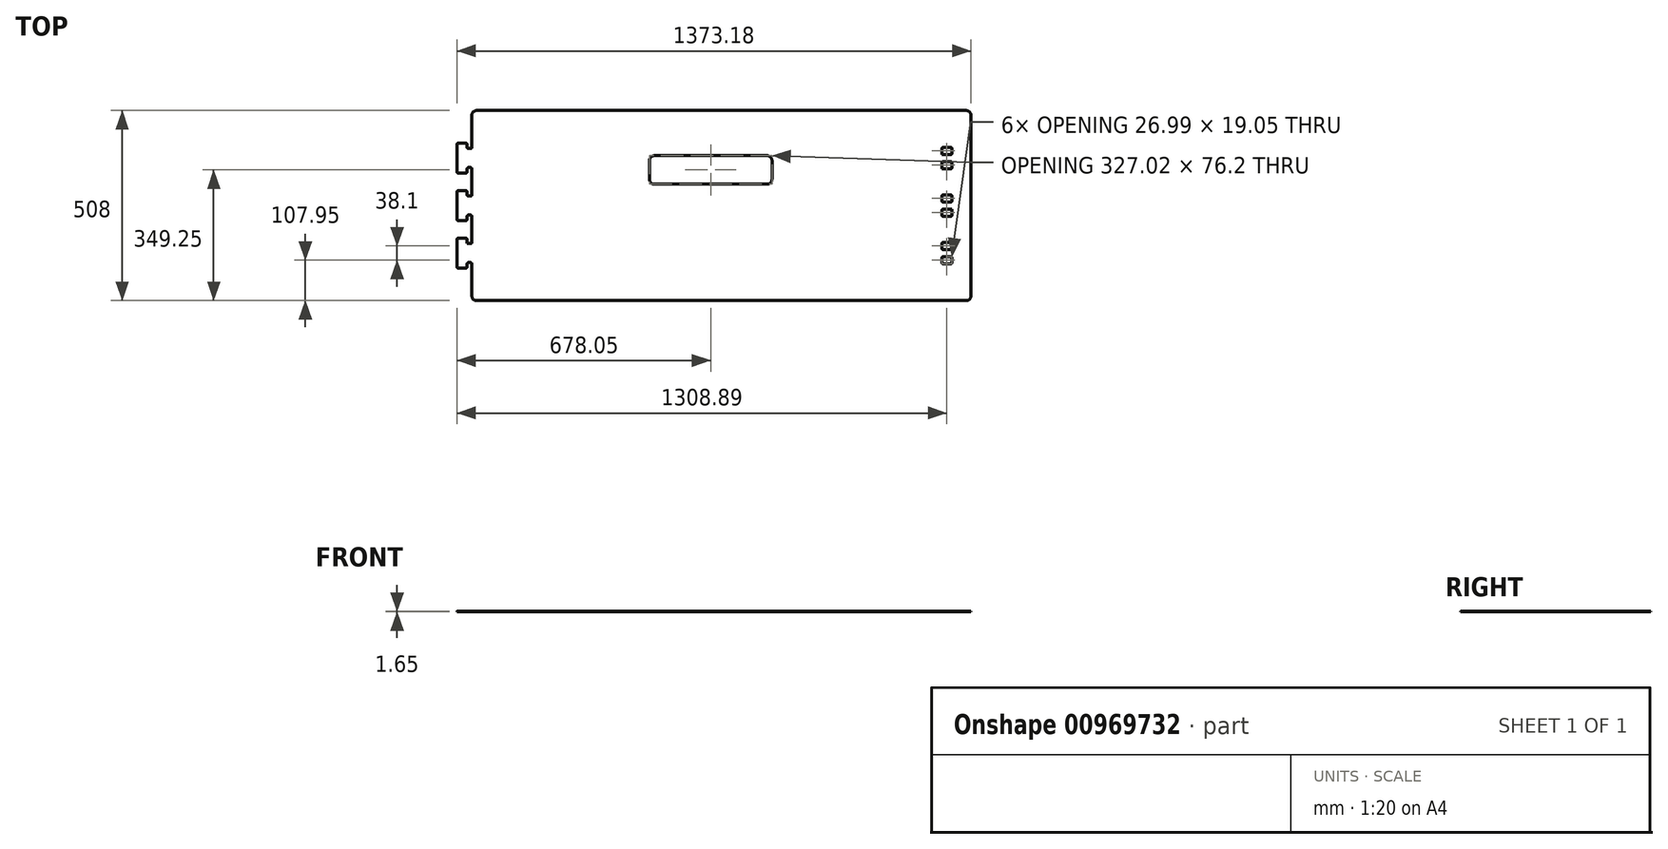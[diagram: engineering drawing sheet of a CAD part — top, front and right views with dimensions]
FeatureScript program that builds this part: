
annotation { "Feature Type Name" : "Feature", "Feature Type Description" : "" }
export const myFeature = defineFeature(function(context is Context, id is Id, definition is map)
    precondition{}
    {
        {
            var Q0;
            Q0=qCreatedBy(makeId("Top.planeOp"),FACE);
            var sketch = newSketch(context, id + "F0", { "sketchPlane" : qUnion([Q0])});
            skLineSegment(sketch, "E0.bottom", {"start": v(-638.37, 254) * mm, "end": v(638.37, 254) * mm});
            skLineSegment(sketch, "E0.top", {"start": v(-638.37, -254) * mm, "end": v(638.37, -254) * mm});
            skLineSegment(sketch, "E0.left", {"start": v(-638.37, 254) * mm, "end": v(-638.37, -254) * mm});
            skPoint(sketch, "E0.middle", {"position": v(0, 0) * mm});
            skLineSegment(sketch, "E1", {"start": v(0, -254) * mm, "end": v(0, 254) * mm, "construction": true});
            skLineSegment(sketch, "E2.bottom", {"start": v(-163.51, 133.35) * mm, "end": v(163.51, 133.35) * mm});
            skLineSegment(sketch, "E2.top", {"start": v(-163.51, 57.15) * mm, "end": v(163.51, 57.15) * mm});
            skLineSegment(sketch, "E2.left", {"start": v(-163.51, 133.35) * mm, "end": v(-163.51, 57.15) * mm});
            skLineSegment(sketch, "E2.right", {"start": v(163.51, 133.35) * mm, "end": v(163.51, 57.15) * mm});
            skPoint(sketch, "E2.middle", {"position": v(0, 95.25) * mm});
            skLineSegment(sketch, "E3.bottom", {"start": v(638.37, 254) * mm, "end": v(695.13, 254) * mm});
            skLineSegment(sketch, "E3.top", {"start": v(638.37, -254) * mm, "end": v(695.13, -254) * mm});
            skLineSegment(sketch, "E3.right", {"start": v(695.13, 254) * mm, "end": v(695.13, -254) * mm});
            skLineSegment(sketch, "E4.bottom", {"start": v(617.35, 155.57) * mm, "end": v(644.33, 155.57) * mm});
            skLineSegment(sketch, "E4.top", {"start": v(617.35, 136.52) * mm, "end": v(644.33, 136.52) * mm});
            skLineSegment(sketch, "E4.left", {"start": v(617.35, 155.57) * mm, "end": v(617.35, 136.52) * mm});
            skLineSegment(sketch, "E4.right", {"start": v(644.33, 155.57) * mm, "end": v(644.33, 136.52) * mm});
            skLineSegment(sketch, "E5", {"start": v(593.26, 127) * mm, "end": v(674.37, 127) * mm, "construction": true});
            skLineSegment(sketch, "E6.MirrorCS", {"start": v(617.35, 98.42) * mm, "end": v(644.33, 98.42) * mm});
            skLineSegment(sketch, "E7.MirrorCS", {"start": v(644.33, 98.42) * mm, "end": v(644.33, 117.47) * mm});
            skLineSegment(sketch, "E8.MirrorCS", {"start": v(617.35, 117.47) * mm, "end": v(644.33, 117.47) * mm});
            skLineSegment(sketch, "E9", {"start": v(617.35, 117.47) * mm, "end": v(617.35, 98.42) * mm});
            skLineSegment(sketch, "E10.0.1.0", {"start": v(617.35, 9.52) * mm, "end": v(644.33, 9.52) * mm});
            skLineSegment(sketch, "E10.0.1.1", {"start": v(617.35, 28.57) * mm, "end": v(644.33, 28.57) * mm});
            skLineSegment(sketch, "E10.0.1.2", {"start": v(617.35, -9.53) * mm, "end": v(617.35, -28.58) * mm});
            skLineSegment(sketch, "E10.0.1.3", {"start": v(617.35, -28.58) * mm, "end": v(644.33, -28.58) * mm});
            skLineSegment(sketch, "E10.0.1.4", {"start": v(617.35, -9.53) * mm, "end": v(644.33, -9.53) * mm});
            skLineSegment(sketch, "E10.0.1.5", {"start": v(644.33, -28.58) * mm, "end": v(644.33, -9.53) * mm});
            skLineSegment(sketch, "E10.0.1.6", {"start": v(617.35, 28.57) * mm, "end": v(617.35, 9.52) * mm});
            skLineSegment(sketch, "E10.0.1.7", {"start": v(644.33, 28.57) * mm, "end": v(644.33, 9.52) * mm});
            skLineSegment(sketch, "E10.0.2.0", {"start": v(617.35, -117.48) * mm, "end": v(644.33, -117.48) * mm});
            skLineSegment(sketch, "E10.0.2.1", {"start": v(617.35, -98.43) * mm, "end": v(644.33, -98.43) * mm});
            skLineSegment(sketch, "E10.0.2.2", {"start": v(617.35, -136.53) * mm, "end": v(617.35, -155.58) * mm});
            skLineSegment(sketch, "E10.0.2.3", {"start": v(617.35, -155.58) * mm, "end": v(644.33, -155.58) * mm});
            skLineSegment(sketch, "E10.0.2.4", {"start": v(617.35, -136.53) * mm, "end": v(644.33, -136.53) * mm});
            skLineSegment(sketch, "E10.0.2.5", {"start": v(644.33, -155.58) * mm, "end": v(644.33, -136.53) * mm});
            skLineSegment(sketch, "E10.0.2.6", {"start": v(617.35, -98.43) * mm, "end": v(617.35, -117.48) * mm});
            skLineSegment(sketch, "E10.0.2.7", {"start": v(644.33, -98.43) * mm, "end": v(644.33, -117.48) * mm});
            skLineSegment(sketch, "E10.direction1", {"start": v(617.35, 98.42) * mm, "end": v(642.75, 98.42) * mm, "construction": true});
            skLineSegment(sketch, "E10.direction2", {"start": v(617.35, 98.42) * mm, "end": v(617.35, -28.58) * mm, "construction": true});
            skLineSegment(sketch, "E11.bottom", {"start": v(-638.37, 152.4) * mm, "end": v(-651.07, 152.4) * mm});
            skLineSegment(sketch, "E11.top", {"start": v(-638.37, 101.6) * mm, "end": v(-651.07, 101.6) * mm});
            skLineSegment(sketch, "E11.left", {"start": v(-638.37, 152.4) * mm, "end": v(-638.37, 101.6) * mm});
            skLineSegment(sketch, "E11.right", {"start": v(-651.07, 152.4) * mm, "end": v(-651.07, 101.6) * mm});
            skLineSegment(sketch, "E12.bottom", {"start": v(-651.07, 166.69) * mm, "end": v(-678.05, 166.69) * mm});
            skLineSegment(sketch, "E12.top", {"start": v(-651.07, 87.31) * mm, "end": v(-678.05, 87.31) * mm});
            skLineSegment(sketch, "E12.left", {"start": v(-651.07, 166.69) * mm, "end": v(-651.07, 87.31) * mm});
            skLineSegment(sketch, "E12.right", {"start": v(-678.05, 166.69) * mm, "end": v(-678.05, 87.31) * mm});
            skPoint(sketch, "E13", {"position": v(-651.07, 127) * mm});
            skLineSegment(sketch, "E14.0.1.0", {"start": v(-638.37, 25.4) * mm, "end": v(-638.37, -25.4) * mm});
            skLineSegment(sketch, "E14.0.1.1", {"start": v(-678.05, 39.69) * mm, "end": v(-678.05, -39.69) * mm});
            skPoint(sketch, "E14.0.1.2", {"position": v(-651.07, 0) * mm});
            skLineSegment(sketch, "E14.0.1.3", {"start": v(-651.07, -39.69) * mm, "end": v(-678.05, -39.69) * mm});
            skLineSegment(sketch, "E14.0.1.4", {"start": v(-651.07, 39.69) * mm, "end": v(-678.05, 39.69) * mm});
            skLineSegment(sketch, "E14.0.1.5", {"start": v(-651.07, 39.69) * mm, "end": v(-651.07, -39.69) * mm});
            skLineSegment(sketch, "E14.0.1.6", {"start": v(-651.07, 25.4) * mm, "end": v(-651.07, -25.4) * mm});
            skPoint(sketch, "E14.0.1.7", {"position": v(-651.07, 0) * mm});
            skLineSegment(sketch, "E14.0.1.8", {"start": v(-638.37, 25.4) * mm, "end": v(-651.07, 25.4) * mm});
            skLineSegment(sketch, "E14.0.1.9", {"start": v(-638.37, -25.4) * mm, "end": v(-651.07, -25.4) * mm});
            skLineSegment(sketch, "E14.0.2.0", {"start": v(-638.37, -101.6) * mm, "end": v(-638.37, -152.4) * mm});
            skLineSegment(sketch, "E14.0.2.1", {"start": v(-678.05, -87.31) * mm, "end": v(-678.05, -166.69) * mm});
            skPoint(sketch, "E14.0.2.2", {"position": v(-651.07, -127) * mm});
            skLineSegment(sketch, "E14.0.2.3", {"start": v(-651.07, -166.69) * mm, "end": v(-678.05, -166.69) * mm});
            skLineSegment(sketch, "E14.0.2.4", {"start": v(-651.07, -87.31) * mm, "end": v(-678.05, -87.31) * mm});
            skLineSegment(sketch, "E14.0.2.5", {"start": v(-651.07, -87.31) * mm, "end": v(-651.07, -166.69) * mm});
            skLineSegment(sketch, "E14.0.2.6", {"start": v(-651.07, -101.6) * mm, "end": v(-651.07, -152.4) * mm});
            skPoint(sketch, "E14.0.2.7", {"position": v(-651.07, -127) * mm});
            skLineSegment(sketch, "E14.0.2.8", {"start": v(-638.37, -101.6) * mm, "end": v(-651.07, -101.6) * mm});
            skLineSegment(sketch, "E14.0.2.9", {"start": v(-638.37, -152.4) * mm, "end": v(-651.07, -152.4) * mm});
            skLineSegment(sketch, "E14.direction1", {"start": v(-678.05, 87.31) * mm, "end": v(-652.65, 87.31) * mm, "construction": true});
            skLineSegment(sketch, "E14.direction2", {"start": v(-678.05, 87.31) * mm, "end": v(-678.05, -39.69) * mm, "construction": true});
            skSolve(sketch);
        }
        {
            var Q0;
            {var subQ3=sQuery(id+"F0.wireOp",EDGE,"E11.bottom");var subQ6=sQuery(id+"F0.wireOp",EDGE,"E11.right");var subQ7=makeQuery(id+"F0.imprint","IMPRINT",EDGE,{"derivedFrom":subQ6});var subQ8=sQuery(id+"F0.wireOp",EDGE,"E14.0.1.8");var subQ22=sQuery(id+"F0.wireOp",EDGE,"E14.0.2.8");var subQ32=sQuery(id+"F0.wireOp",EDGE,"E0.bottom");Q0=qUnion([makeQuery(id+"F0.imprint","IMPRINT",FACE,{"disambiguationData":[TD([[makeQuery(id+"F0.imprint","IMPRINT",EDGE,{"derivedFrom":sQuery(id+"F0.wireOp",EDGE,"E14.0.2.1")}),1.0]])]}),makeQuery(id+"F0.imprint","IMPRINT",FACE,{"disambiguationData":[TD([[makeQuery(id+"F0.imprint","IMPRINT",EDGE,{"derivedFrom":subQ32}),-1.0]])]}),makeQuery(id+"F0.imprint","IMPRINT",FACE,{"disambiguationData":[TD([[makeQuery(id+"F0.imprint","IMPRINT",EDGE,{"derivedFrom":subQ22}),1.0]])]}),makeQuery(id+"F0.imprint","IMPRINT",FACE,{"disambiguationData":[TD([[subQ7,-1.0]])]}),makeQuery(id+"F0.imprint","IMPRINT",FACE,{"disambiguationData":[TD([[makeQuery(id+"F0.imprint","IMPRINT",EDGE,{"derivedFrom":subQ8}),1.0]])]}),makeQuery(id+"F0.imprint","IMPRINT",FACE,{"disambiguationData":[TD([[makeQuery(id+"F0.imprint","IMPRINT",EDGE,{"derivedFrom":sQuery(id+"F0.wireOp",EDGE,"E14.0.1.1")}),1.0]])]}),makeQuery(id+"F0.imprint","IMPRINT",FACE,{"disambiguationData":[TD([[makeQuery(id+"F0.imprint","IMPRINT",EDGE,{"derivedFrom":subQ3}),1.0]])]})]);}
            extrude(context, id + "F1", {"entities" : qUnion([Q0]), "depth" : 1.65 * mm, "offsetDistance" : 25.4 * mm});
        }
        {
            var Q0;
            Q0=makeQuery(id+"F1.opExtrude","SWEPT_EDGE",EDGE,{"disambiguationData":[OSD([sQuery(id+"F0.wireOp",EDGE,"E2.bottom"),sQuery(id+"F0.wireOp",EDGE,"E2.left")])]});
            var Q1;
            Q1=makeQuery(id+"F1.opExtrude","SWEPT_EDGE",EDGE,{"disambiguationData":[OSD([sQuery(id+"F0.wireOp",EDGE,"E2.bottom"),sQuery(id+"F0.wireOp",EDGE,"E2.right")])]});
            var Q2;
            Q2=makeQuery(id+"F1.opExtrude","SWEPT_EDGE",EDGE,{"disambiguationData":[OSD([sQuery(id+"F0.wireOp",EDGE,"E2.top"),sQuery(id+"F0.wireOp",EDGE,"E2.left")])]});
            var Q3;
            Q3=makeQuery(id+"F1.opExtrude","SWEPT_EDGE",EDGE,{"disambiguationData":[OSD([sQuery(id+"F0.wireOp",EDGE,"E2.top"),sQuery(id+"F0.wireOp",EDGE,"E2.right")])]});
            fillet(context, id + "F2", {"entities" : qUnion([Q0, Q1, Q2, Q3]), "radius" : 12.7 * mm, "tangentPropagation" : true, "allowEdgeOverflow" : false});
        }
        {
            var Q0;
            Q0=makeQuery(id+"F1.opExtrude","SWEPT_EDGE",EDGE,{"disambiguationData":[OSD([sQuery(id+"F0.wireOp",EDGE,"E12.bottom"),sQuery(id+"F0.wireOp",EDGE,"E12.right")])]});
            var Q1;
            Q1=makeQuery(id+"F1.opExtrude","SWEPT_EDGE",EDGE,{"disambiguationData":[OSD([sQuery(id+"F0.wireOp",EDGE,"E12.bottom"),sQuery(id+"F0.wireOp",EDGE,"E12.left")])]});
            var Q2;
            Q2=makeQuery(id+"F1.opExtrude","SWEPT_EDGE",EDGE,{"disambiguationData":[OSD([sQuery(id+"F0.wireOp",EDGE,"E0.left"),sQuery(id+"F0.wireOp",EDGE,"E11.bottom")])]});
            var Q3;
            Q3=makeQuery(id+"F1.opExtrude","SWEPT_EDGE",EDGE,{"disambiguationData":[OSD([sQuery(id+"F0.wireOp",EDGE,"E11.bottom"),sQuery(id+"F0.wireOp",EDGE,"E11.right"),sQuery(id+"F0.wireOp",EDGE,"E12.left")])]});
            var Q4;
            Q4=makeQuery(id+"F1.opExtrude","SWEPT_EDGE",EDGE,{"disambiguationData":[OSD([sQuery(id+"F0.wireOp",EDGE,"E12.top"),sQuery(id+"F0.wireOp",EDGE,"E12.left")])]});
            var Q5;
            Q5=makeQuery(id+"F1.opExtrude","SWEPT_EDGE",EDGE,{"disambiguationData":[OSD([sQuery(id+"F0.wireOp",EDGE,"E11.top"),sQuery(id+"F0.wireOp",EDGE,"E11.right"),sQuery(id+"F0.wireOp",EDGE,"E12.left")])]});
            var Q6;
            Q6=makeQuery(id+"F1.opExtrude","SWEPT_EDGE",EDGE,{"disambiguationData":[OSD([sQuery(id+"F0.wireOp",EDGE,"E12.top"),sQuery(id+"F0.wireOp",EDGE,"E12.right")])]});
            var Q7;
            Q7=makeQuery(id+"F1.opExtrude","SWEPT_EDGE",EDGE,{"disambiguationData":[OSD([sQuery(id+"F0.wireOp",EDGE,"E0.left"),sQuery(id+"F0.wireOp",EDGE,"E11.top")])]});
            var Q8;
            Q8=makeQuery(id+"F1.opExtrude","SWEPT_EDGE",EDGE,{"disambiguationData":[OSD([sQuery(id+"F0.wireOp",EDGE,"E0.left"),sQuery(id+"F0.wireOp",EDGE,"E14.0.1.9")])]});
            var Q9;
            Q9=makeQuery(id+"F1.opExtrude","SWEPT_EDGE",EDGE,{"disambiguationData":[OSD([sQuery(id+"F0.wireOp",EDGE,"E0.left"),sQuery(id+"F0.wireOp",EDGE,"E14.0.1.8")])]});
            var Q10;
            Q10=makeQuery(id+"F1.opExtrude","SWEPT_EDGE",EDGE,{"disambiguationData":[OSD([sQuery(id+"F0.wireOp",EDGE,"E14.0.1.4"),sQuery(id+"F0.wireOp",EDGE,"E14.0.1.5")])]});
            var Q11;
            Q11=makeQuery(id+"F1.opExtrude","SWEPT_EDGE",EDGE,{"disambiguationData":[OSD([sQuery(id+"F0.wireOp",EDGE,"E14.0.1.5"),sQuery(id+"F0.wireOp",EDGE,"E14.0.1.8")])]});
            var Q12;
            Q12=makeQuery(id+"F1.opExtrude","SWEPT_EDGE",EDGE,{"disambiguationData":[OSD([sQuery(id+"F0.wireOp",EDGE,"E14.0.1.1"),sQuery(id+"F0.wireOp",EDGE,"E14.0.1.4")])]});
            var Q13;
            Q13=makeQuery(id+"F1.opExtrude","SWEPT_EDGE",EDGE,{"disambiguationData":[OSD([sQuery(id+"F0.wireOp",EDGE,"E14.0.1.1"),sQuery(id+"F0.wireOp",EDGE,"E14.0.1.3")])]});
            var Q14;
            Q14=makeQuery(id+"F1.opExtrude","SWEPT_EDGE",EDGE,{"disambiguationData":[OSD([sQuery(id+"F0.wireOp",EDGE,"E14.0.1.3"),sQuery(id+"F0.wireOp",EDGE,"E14.0.1.5")])]});
            var Q15;
            Q15=makeQuery(id+"F1.opExtrude","SWEPT_EDGE",EDGE,{"disambiguationData":[OSD([sQuery(id+"F0.wireOp",EDGE,"E14.0.1.5"),sQuery(id+"F0.wireOp",EDGE,"E14.0.1.9")])]});
            var Q16;
            Q16=makeQuery(id+"F1.opExtrude","SWEPT_EDGE",EDGE,{"disambiguationData":[OSD([sQuery(id+"F0.wireOp",EDGE,"E0.left"),sQuery(id+"F0.wireOp",EDGE,"E14.0.2.8")])]});
            var Q17;
            Q17=makeQuery(id+"F1.opExtrude","SWEPT_EDGE",EDGE,{"disambiguationData":[OSD([sQuery(id+"F0.wireOp",EDGE,"E14.0.2.4"),sQuery(id+"F0.wireOp",EDGE,"E14.0.2.5")])]});
            var Q18;
            Q18=makeQuery(id+"F1.opExtrude","SWEPT_EDGE",EDGE,{"disambiguationData":[OSD([sQuery(id+"F0.wireOp",EDGE,"E14.0.2.1"),sQuery(id+"F0.wireOp",EDGE,"E14.0.2.4")])]});
            var Q19;
            Q19=makeQuery(id+"F1.opExtrude","SWEPT_EDGE",EDGE,{"disambiguationData":[OSD([sQuery(id+"F0.wireOp",EDGE,"E14.0.2.1"),sQuery(id+"F0.wireOp",EDGE,"E14.0.2.3")])]});
            var Q20;
            Q20=makeQuery(id+"F1.opExtrude","SWEPT_EDGE",EDGE,{"disambiguationData":[OSD([sQuery(id+"F0.wireOp",EDGE,"E14.0.2.3"),sQuery(id+"F0.wireOp",EDGE,"E14.0.2.5")])]});
            var Q21;
            Q21=makeQuery(id+"F1.opExtrude","SWEPT_EDGE",EDGE,{"disambiguationData":[OSD([sQuery(id+"F0.wireOp",EDGE,"E0.left"),sQuery(id+"F0.wireOp",EDGE,"E14.0.2.9")])]});
            var Q22;
            Q22=makeQuery(id+"F1.opExtrude","SWEPT_EDGE",EDGE,{"disambiguationData":[OSD([sQuery(id+"F0.wireOp",EDGE,"E14.0.2.5"),sQuery(id+"F0.wireOp",EDGE,"E14.0.2.9")])]});
            var Q23;
            Q23=makeQuery(id+"F1.opExtrude","SWEPT_EDGE",EDGE,{"disambiguationData":[OSD([sQuery(id+"F0.wireOp",EDGE,"E4.bottom"),sQuery(id+"F0.wireOp",EDGE,"E4.left")])]});
            var Q24;
            Q24=makeQuery(id+"F1.opExtrude","SWEPT_EDGE",EDGE,{"disambiguationData":[OSD([sQuery(id+"F0.wireOp",EDGE,"E8.MirrorCS"),sQuery(id+"F0.wireOp",EDGE,"E9")])]});
            var Q25;
            Q25=makeQuery(id+"F1.opExtrude","SWEPT_EDGE",EDGE,{"disambiguationData":[OSD([sQuery(id+"F0.wireOp",EDGE,"E10.0.1.1"),sQuery(id+"F0.wireOp",EDGE,"E10.0.1.6")])]});
            var Q26;
            Q26=makeQuery(id+"F1.opExtrude","SWEPT_EDGE",EDGE,{"disambiguationData":[OSD([sQuery(id+"F0.wireOp",EDGE,"E10.0.2.2"),sQuery(id+"F0.wireOp",EDGE,"E10.0.2.4")])]});
            var Q27;
            Q27=makeQuery(id+"F1.opExtrude","SWEPT_EDGE",EDGE,{"disambiguationData":[OSD([sQuery(id+"F0.wireOp",EDGE,"E10.0.2.1"),sQuery(id+"F0.wireOp",EDGE,"E10.0.2.6")])]});
            var Q28;
            Q28=makeQuery(id+"F1.opExtrude","SWEPT_EDGE",EDGE,{"disambiguationData":[OSD([sQuery(id+"F0.wireOp",EDGE,"E10.0.1.2"),sQuery(id+"F0.wireOp",EDGE,"E10.0.1.4")])]});
            var Q29;
            Q29=makeQuery(id+"F1.opExtrude","SWEPT_EDGE",EDGE,{"disambiguationData":[OSD([sQuery(id+"F0.wireOp",EDGE,"E10.0.1.0"),sQuery(id+"F0.wireOp",EDGE,"E10.0.1.6")])]});
            var Q30;
            Q30=makeQuery(id+"F1.opExtrude","SWEPT_EDGE",EDGE,{"disambiguationData":[OSD([sQuery(id+"F0.wireOp",EDGE,"E10.0.1.2"),sQuery(id+"F0.wireOp",EDGE,"E10.0.1.3")])]});
            var Q31;
            Q31=makeQuery(id+"F1.opExtrude","SWEPT_EDGE",EDGE,{"disambiguationData":[OSD([sQuery(id+"F0.wireOp",EDGE,"E10.0.2.0"),sQuery(id+"F0.wireOp",EDGE,"E10.0.2.6")])]});
            var Q32;
            Q32=makeQuery(id+"F1.opExtrude","SWEPT_EDGE",EDGE,{"disambiguationData":[OSD([sQuery(id+"F0.wireOp",EDGE,"E10.0.2.2"),sQuery(id+"F0.wireOp",EDGE,"E10.0.2.3")])]});
            var Q33;
            Q33=makeQuery(id+"F1.opExtrude","SWEPT_EDGE",EDGE,{"disambiguationData":[OSD([sQuery(id+"F0.wireOp",EDGE,"E10.0.2.3"),sQuery(id+"F0.wireOp",EDGE,"E10.0.2.5")])]});
            var Q34;
            Q34=makeQuery(id+"F1.opExtrude","SWEPT_EDGE",EDGE,{"disambiguationData":[OSD([sQuery(id+"F0.wireOp",EDGE,"E10.0.2.4"),sQuery(id+"F0.wireOp",EDGE,"E10.0.2.5")])]});
            var Q35;
            Q35=makeQuery(id+"F1.opExtrude","SWEPT_EDGE",EDGE,{"disambiguationData":[OSD([sQuery(id+"F0.wireOp",EDGE,"E10.0.2.1"),sQuery(id+"F0.wireOp",EDGE,"E10.0.2.7")])]});
            var Q36;
            Q36=makeQuery(id+"F1.opExtrude","SWEPT_EDGE",EDGE,{"disambiguationData":[OSD([sQuery(id+"F0.wireOp",EDGE,"E4.bottom"),sQuery(id+"F0.wireOp",EDGE,"E4.right")])]});
            var Q37;
            Q37=makeQuery(id+"F1.opExtrude","SWEPT_EDGE",EDGE,{"disambiguationData":[OSD([sQuery(id+"F0.wireOp",EDGE,"E7.MirrorCS"),sQuery(id+"F0.wireOp",EDGE,"E8.MirrorCS")])]});
            var Q38;
            Q38=makeQuery(id+"F1.opExtrude","SWEPT_EDGE",EDGE,{"disambiguationData":[OSD([sQuery(id+"F0.wireOp",EDGE,"E6.MirrorCS"),sQuery(id+"F0.wireOp",EDGE,"E7.MirrorCS")])]});
            var Q39;
            Q39=makeQuery(id+"F1.opExtrude","SWEPT_EDGE",EDGE,{"disambiguationData":[OSD([sQuery(id+"F0.wireOp",EDGE,"E10.0.1.0"),sQuery(id+"F0.wireOp",EDGE,"E10.0.1.7")])]});
            var Q40;
            Q40=makeQuery(id+"F1.opExtrude","SWEPT_EDGE",EDGE,{"disambiguationData":[OSD([sQuery(id+"F0.wireOp",EDGE,"E4.top"),sQuery(id+"F0.wireOp",EDGE,"E4.right")])]});
            var Q41;
            Q41=makeQuery(id+"F1.opExtrude","SWEPT_EDGE",EDGE,{"disambiguationData":[OSD([sQuery(id+"F0.wireOp",EDGE,"E10.0.1.3"),sQuery(id+"F0.wireOp",EDGE,"E10.0.1.5")])]});
            var Q42;
            Q42=makeQuery(id+"F1.opExtrude","SWEPT_EDGE",EDGE,{"disambiguationData":[OSD([sQuery(id+"F0.wireOp",EDGE,"E10.0.1.1"),sQuery(id+"F0.wireOp",EDGE,"E10.0.1.7")])]});
            var Q43;
            Q43=makeQuery(id+"F1.opExtrude","SWEPT_EDGE",EDGE,{"disambiguationData":[OSD([sQuery(id+"F0.wireOp",EDGE,"E10.0.2.0"),sQuery(id+"F0.wireOp",EDGE,"E10.0.2.7")])]});
            fillet(context, id + "F3", {"entities" : qUnion([Q0, Q1, Q2, Q3, Q4, Q5, Q6, Q7, Q8, Q9, Q10, Q11, Q12, Q13, Q14, Q15, Q16, Q17, Q18, Q19, Q20, Q21, Q22, Q23, Q24, Q25, Q26, Q27, Q28, Q29, Q30, Q31, Q32, Q33, Q34, Q35, Q36, Q37, Q38, Q39, Q40, Q41, Q42, Q43]), "radius" : 3.17 * mm, "tangentPropagation" : true, "allowEdgeOverflow" : false});
        }
        {
            var Q0;
            Q0=makeQuery(id+"F1.opExtrude","SWEPT_EDGE",EDGE,{"disambiguationData":[OSD([sQuery(id+"F0.wireOp",EDGE,"E3.bottom"),sQuery(id+"F0.wireOp",EDGE,"E3.right")])]});
            var Q1;
            Q1=makeQuery(id+"F1.opExtrude","SWEPT_EDGE",EDGE,{"disambiguationData":[OSD([sQuery(id+"F0.wireOp",EDGE,"E3.top"),sQuery(id+"F0.wireOp",EDGE,"E3.right")])]});
            var Q2;
            Q2=makeQuery(id+"F1.opExtrude","SWEPT_EDGE",EDGE,{"disambiguationData":[OSD([sQuery(id+"F0.wireOp",EDGE,"E0.top"),sQuery(id+"F0.wireOp",EDGE,"E0.left")])]});
            var Q3;
            Q3=makeQuery(id+"F1.opExtrude","SWEPT_EDGE",EDGE,{"disambiguationData":[OSD([sQuery(id+"F0.wireOp",EDGE,"E0.bottom"),sQuery(id+"F0.wireOp",EDGE,"E0.left")])]});
            fillet(context, id + "F4", {"entities" : qUnion([Q0, Q1, Q2, Q3]), "radius" : 12.7 * mm, "tangentPropagation" : true, "allowEdgeOverflow" : false});
        }
    });
